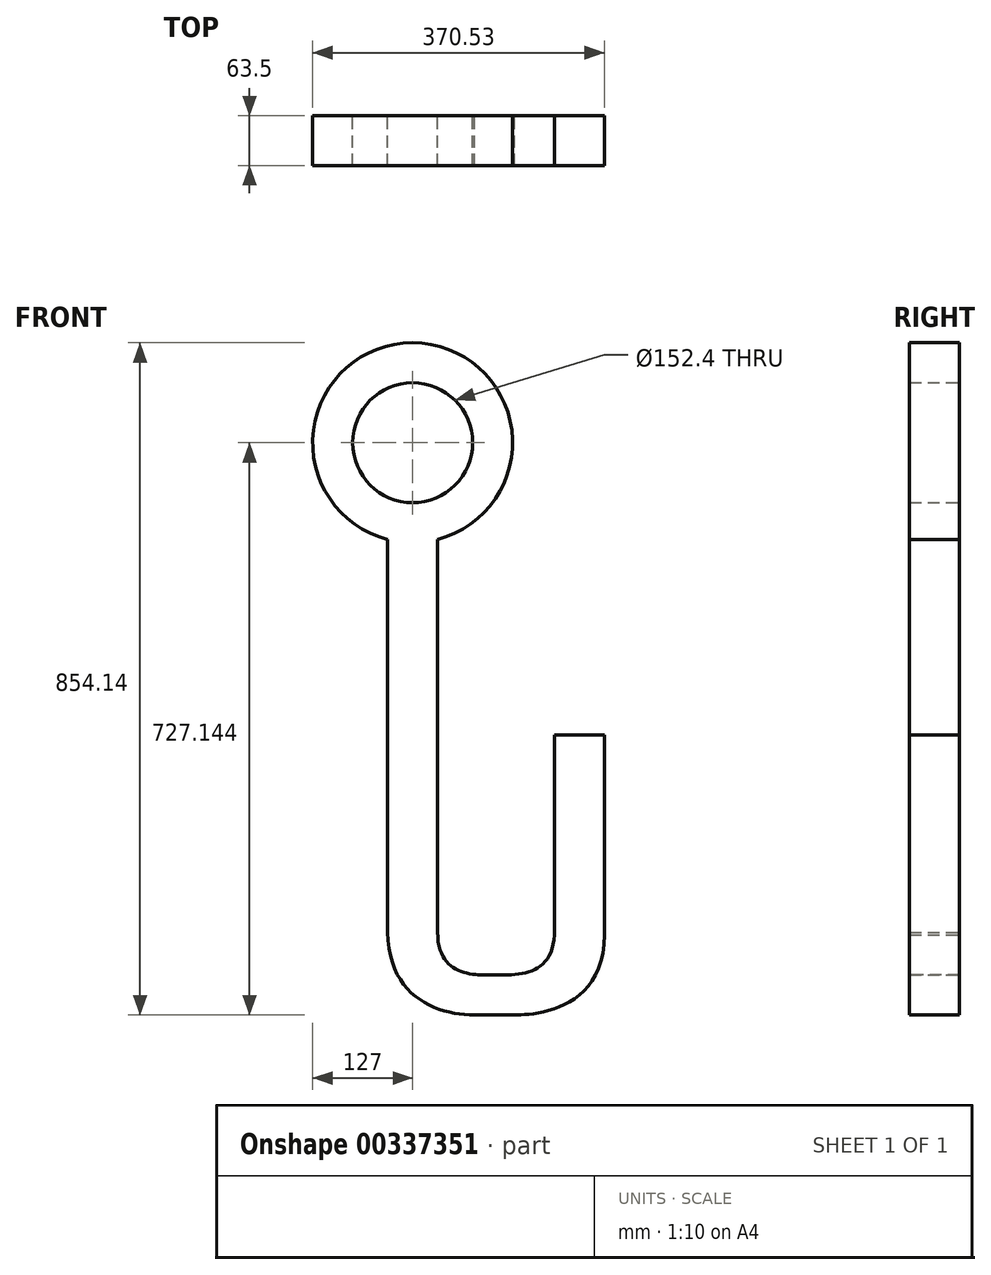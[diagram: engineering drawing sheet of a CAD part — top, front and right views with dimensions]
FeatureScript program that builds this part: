
annotation { "Feature Type Name" : "Feature", "Feature Type Description" : "" }
export const myFeature = defineFeature(function(context is Context, id is Id, definition is map)
    precondition{}
    {
        {
            var Q0;
            Q0=qCreatedBy(makeId("Front.planeOp"),FACE);
            var sketch = newSketch(context, id + "F0", { "sketchPlane" : qUnion([Q0])});
            skLineSegment(sketch, "E0.bottom", {"start": v(-31.75, -495.17) * mm, "end": v(31.75, -495.17) * mm});
            skLineSegment(sketch, "E0.top", {"start": v(-31.75, 12.83) * mm, "end": v(31.75, 12.83) * mm});
            skLineSegment(sketch, "E0.left", {"start": v(-31.75, -495.17) * mm, "end": v(-31.75, 12.83) * mm});
            skLineSegment(sketch, "E0.right", {"start": v(31.75, -495.17) * mm, "end": v(31.75, 12.83) * mm});
            skPoint(sketch, "E0.middle", {"position": v(0, -241.17) * mm});
            skLineSegment(sketch, "E1.bottom", {"start": v(78.43, -549.66) * mm, "end": v(129.23, -549.66) * mm});
            skLineSegment(sketch, "E1.top", {"start": v(78.43, -600.46) * mm, "end": v(129.23, -600.46) * mm});
            skLineSegment(sketch, "E1.left", {"start": v(78.43, -549.66) * mm, "end": v(78.43, -600.46) * mm});
            skLineSegment(sketch, "E1.right", {"start": v(129.23, -549.66) * mm, "end": v(129.23, -600.46) * mm});
            skPoint(sketch, "E1.middle", {"position": v(103.83, -575.06) * mm});
            skLineSegment(sketch, "E2.bottom", {"start": v(243.53, -498.86) * mm, "end": v(180.03, -498.86) * mm});
            skLineSegment(sketch, "E2.top", {"start": v(243.53, -244.86) * mm, "end": v(180.03, -244.86) * mm});
            skLineSegment(sketch, "E2.left", {"start": v(243.53, -498.86) * mm, "end": v(243.53, -244.86) * mm});
            skLineSegment(sketch, "E2.right", {"start": v(180.03, -498.86) * mm, "end": v(180.03, -244.86) * mm});
            skPoint(sketch, "E2.middle", {"position": v(211.78, -371.86) * mm});
            skFitSpline(sketch, "E3", {"points": [v(31.75, -495.17) * mm, v(103.83, -549.66) * mm], "startDerivative": vector(0.4, -171) * mm, "endDerivative": vector(76.2, 0) * mm});
            skPoint(sketch, "E4", {"position": v(36.86, -552.17) * mm});
            skFitSpline(sketch, "E5", {"points": [v(-31.75, -495.17) * mm, v(78.43, -600.46) * mm], "startDerivative": vector(5.36, -250.3) * mm, "endDerivative": vector(141.38, -2.2) * mm});
            skFitSpline(sketch, "E6", {"points": [v(103.83, -549.66) * mm, v(180.03, -498.86) * mm], "startDerivative": vector(98.19, 0) * mm, "endDerivative": vector(7.14, 152.34) * mm});
            skFitSpline(sketch, "E7", {"points": [v(129.23, -600.46) * mm, v(243.53, -498.86) * mm], "startDerivative": vector(78.77, 0.89) * mm, "endDerivative": vector(0.79, 287.62) * mm});
            skCircle(sketch, "E8", {"center": v(0, 126.68) * mm, "radius": 127 * mm});
            skCircle(sketch, "E9", {"center": v(0, 126.68) * mm, "radius": 76.2 * mm});
            skSolve(sketch);
        }
        {
            var Q0;
            {var subQ5=sQuery(id+"F0.wireOp",EDGE,"E0.top");Q0=makeQuery(id+"F0.imprint","IMPRINT",FACE,{"disambiguationData":[TD([[makeQuery(id+"F0.imprint","IMPRINT",EDGE,{"derivedFrom":subQ5}),1.0]])]});}
            var Q1;
            {var subQ0=sQuery(id+"F0.wireOp",EDGE,"E0.top");Q1=makeQuery(id+"F0.imprint","IMPRINT",FACE,{"disambiguationData":[TD([[makeQuery(id+"F0.imprint","IMPRINT",EDGE,{"derivedFrom":subQ0}),-1.0]])]});}
            var Q2;
            {var subQ0=sQuery(id+"F0.wireOp",EDGE,"E0.bottom");Q2=makeQuery(id+"F0.imprint","IMPRINT",FACE,{"disambiguationData":[TD([[makeQuery(id+"F0.imprint","IMPRINT",EDGE,{"derivedFrom":subQ0}),1.0]])]});}
            var Q3;
            Q3=makeQuery(id+"F0.imprint","IMPRINT",FACE,{"disambiguationData":[TD([[makeQuery(id+"F0.imprint","IMPRINT",EDGE,{"derivedFrom":sQuery(id+"F0.wireOp",EDGE,"E0.bottom")}),-1.0]])]});
            var Q4;
            Q4=makeQuery(id+"F0.imprint","IMPRINT",FACE,{"disambiguationData":[TD([[makeQuery(id+"F0.imprint","IMPRINT",EDGE,{"derivedFrom":sQuery(id+"F0.wireOp",EDGE,"E1.top")}),1.0]])]});
            var Q5;
            {var subQ0=sQuery(id+"F0.wireOp",EDGE,"E1.right");Q5=makeQuery(id+"F0.imprint","IMPRINT",FACE,{"disambiguationData":[TD([[makeQuery(id+"F0.imprint","IMPRINT",EDGE,{"derivedFrom":subQ0}),1.0]])]});}
            var Q6;
            Q6=makeQuery(id+"F0.imprint","IMPRINT",FACE,{"disambiguationData":[TD([[makeQuery(id+"F0.imprint","IMPRINT",EDGE,{"derivedFrom":sQuery(id+"F0.wireOp",EDGE,"E2.bottom")}),-1.0]])]});
            extrude(context, id + "F1", {"entities" : qUnion([Q0, Q1, Q2, Q3, Q4, Q5, Q6]), "endBound" : BoundingType.SYMMETRIC, "depth" : 63.5 * mm});
        }
    });
